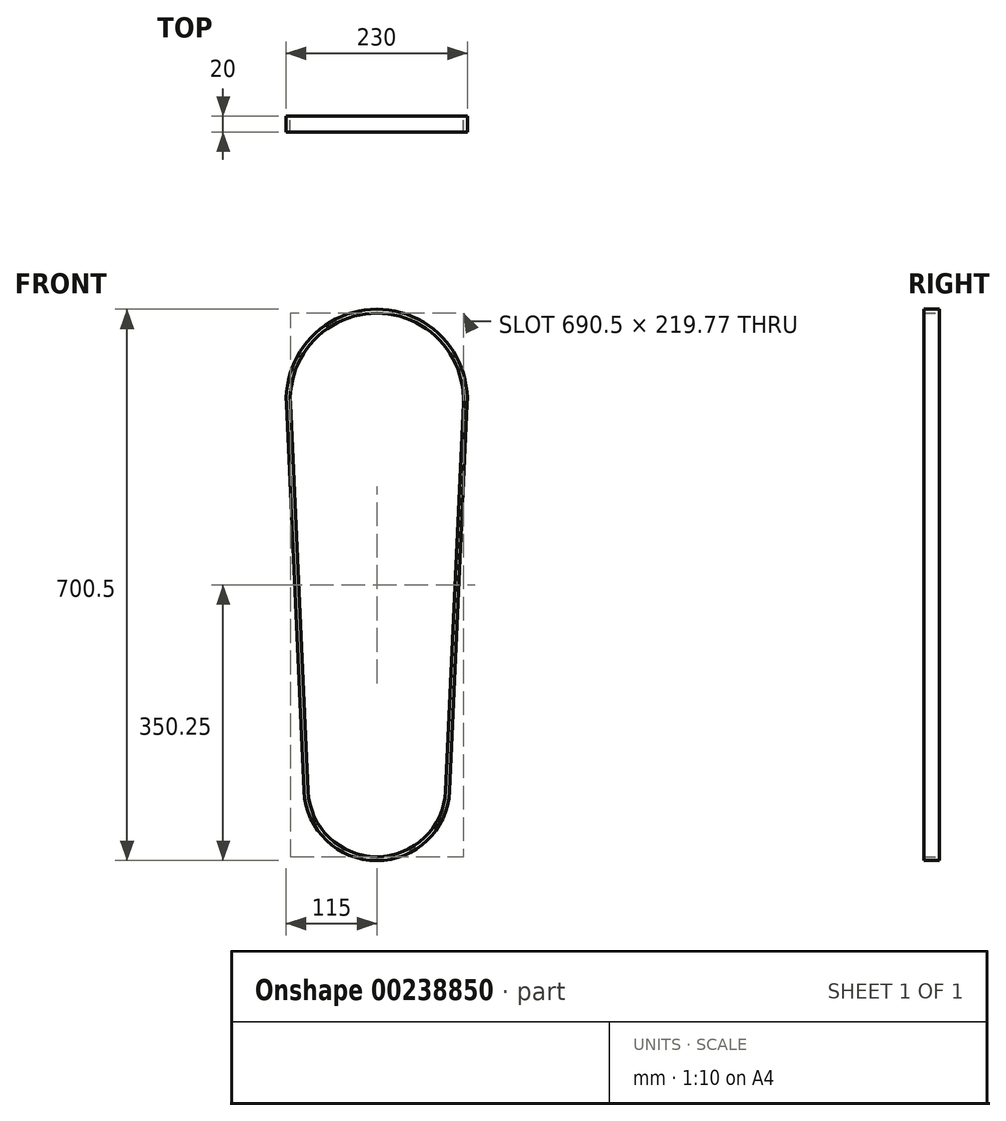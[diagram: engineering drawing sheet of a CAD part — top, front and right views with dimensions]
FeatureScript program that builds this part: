
annotation { "Feature Type Name" : "Feature", "Feature Type Description" : "" }
export const myFeature = defineFeature(function(context is Context, id is Id, definition is map)
    precondition{}
    {
        {
            var Q0;
            Q0=qCreatedBy(makeId("Front.planeOp"),FACE);
            var sketch = newSketch(context, id + "F0", { "sketchPlane" : qUnion([Q0])});
            skArc(sketch, "E0", {"start": v(109.89, -5.02) * mm, "mid": v(0, 110) * mm, "end": v(-109.89, -5.02) * mm});
            skArc(sketch, "E1", {"start": v(-87.4, -497) * mm, "mid": v(0, -580.5) * mm, "end": v(87.4, -497) * mm});
            skLineSegment(sketch, "E2", {"start": v(-109.89, -5.02) * mm, "end": v(-87.4, -497) * mm});
            skLineSegment(sketch, "E3", {"start": v(109.89, -5.02) * mm, "end": v(87.4, -497) * mm});
            skArc(sketch, "E4.0", {"start": v(114.88, -5.25) * mm, "mid": v(0, 115) * mm, "end": v(-114.88, -5.25) * mm});
            skLineSegment(sketch, "E4.1", {"start": v(114.88, -5.25) * mm, "end": v(92.4, -497.22) * mm});
            skArc(sketch, "E4.2", {"start": v(-92.4, -497.22) * mm, "mid": v(0, -585.5) * mm, "end": v(92.4, -497.22) * mm});
            skLineSegment(sketch, "E4.3", {"start": v(-114.88, -5.25) * mm, "end": v(-92.4, -497.22) * mm});
            skSolve(sketch);
        }
        {
            var Q0;
            Q0=makeQuery(id+"F0.imprint","IMPRINT",FACE,{"disambiguationData":[TD([[makeQuery(id+"F0.imprint","IMPRINT",EDGE,{"derivedFrom":sQuery(id+"F0.wireOp",EDGE,"E0")}),-1.0]])]});
            extrude(context, id + "F1", {"entities" : qUnion([Q0]), "depth" : 20 * mm});
        }
    });
